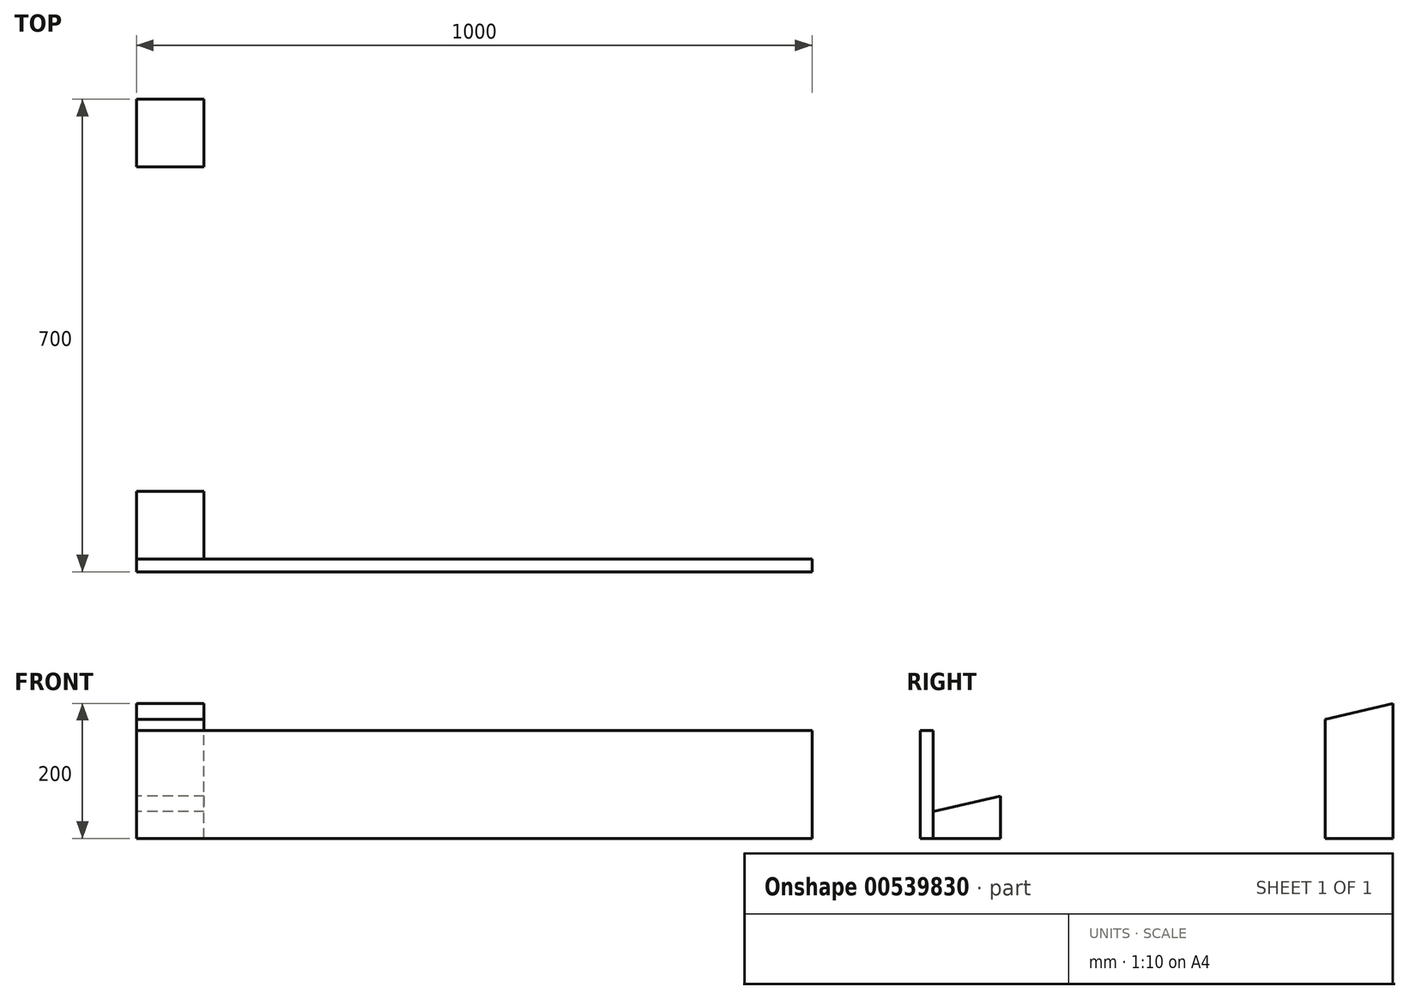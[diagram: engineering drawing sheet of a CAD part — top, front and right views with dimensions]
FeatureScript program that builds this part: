
annotation { "Feature Type Name" : "Feature", "Feature Type Description" : "" }
export const myFeature = defineFeature(function(context is Context, id is Id, definition is map)
    precondition{}
    {
        {
            var Q0;
            Q0=qCreatedBy(makeId("Right.planeOp"),FACE);
            var sketch = newSketch(context, id + "F0", { "sketchPlane" : qUnion([Q0])});
            skLineSegment(sketch, "E0", {"start": v(0, 0) * mm, "end": v(0, 40) * mm});
            skLineSegment(sketch, "E1", {"start": v(681, 0) * mm, "end": v(681, 200) * mm});
            skLineSegment(sketch, "E2", {"start": v(681, 0) * mm, "end": v(581, 0) * mm});
            skLineSegment(sketch, "E3", {"start": v(581, 0) * mm, "end": v(581, 177.14) * mm});
            skLineSegment(sketch, "E4", {"start": v(0, 0) * mm, "end": v(100, 0) * mm});
            skLineSegment(sketch, "E5", {"start": v(100, 0) * mm, "end": v(100, 62.86) * mm});
            skLineSegment(sketch, "E6", {"start": v(581, 177.14) * mm, "end": v(681, 200) * mm});
            skLineSegment(sketch, "E7", {"start": v(100, 62.86) * mm, "end": v(0, 40) * mm});
            skLineSegment(sketch, "E8", {"start": v(0, 40) * mm, "end": v(681, 200) * mm});
            skLineSegment(sketch, "E9", {"start": v(681, 200) * mm, "end": v(676.65, 218.5) * mm});
            skLineSegment(sketch, "E10", {"start": v(676.65, 218.5) * mm, "end": v(0, 59.52) * mm});
            skLineSegment(sketch, "E11.bottom", {"start": v(0, 0) * mm, "end": v(-19, 0) * mm});
            skLineSegment(sketch, "E11.top", {"start": v(0, 160) * mm, "end": v(-19, 160) * mm});
            skLineSegment(sketch, "E11.left", {"start": v(0, 0) * mm, "end": v(0, 160) * mm});
            skLineSegment(sketch, "E11.right", {"start": v(-19, 0) * mm, "end": v(-19, 160) * mm});
            skSolve(sketch);
        }
        {
            var Q0;
            {var subQ0=sQuery(id+"F0.wireOp",EDGE,"E1");Q0=makeQuery(id+"F0.imprint","IMPRINT",FACE,{"disambiguationData":[TD([[makeQuery(id+"F0.imprint","IMPRINT",EDGE,{"derivedFrom":subQ0}),1.0]])]});}
            extrude(context, id + "F1", {"entities" : qUnion([Q0]), "depth" : 100 * mm, "offsetDistance" : 25 * mm});
        }
        {
            var Q0;
            {var subQ0=sQuery(id+"F0.wireOp",EDGE,"E4");Q0=makeQuery(id+"F0.imprint","IMPRINT",FACE,{"disambiguationData":[TD([[makeQuery(id+"F0.imprint","IMPRINT",EDGE,{"derivedFrom":subQ0}),1.0]])]});}
            extrude(context, id + "F2", {"entities" : qUnion([Q0]), "depth" : 100 * mm, "offsetDistance" : 25 * mm});
        }
        {
            var Q0;
            {var subQ3=sQuery(id+"F0.wireOp",EDGE,"E11.bottom");Q0=makeQuery(id+"F0.imprint","IMPRINT",FACE,{"disambiguationData":[TD([[makeQuery(id+"F0.imprint","IMPRINT",EDGE,{"derivedFrom":subQ3}),-1.0]])]});}
            extrude(context, id + "F3", {"entities" : qUnion([Q0]), "depth" : 1000 * mm, "offsetDistance" : 25 * mm});
        }
    });
